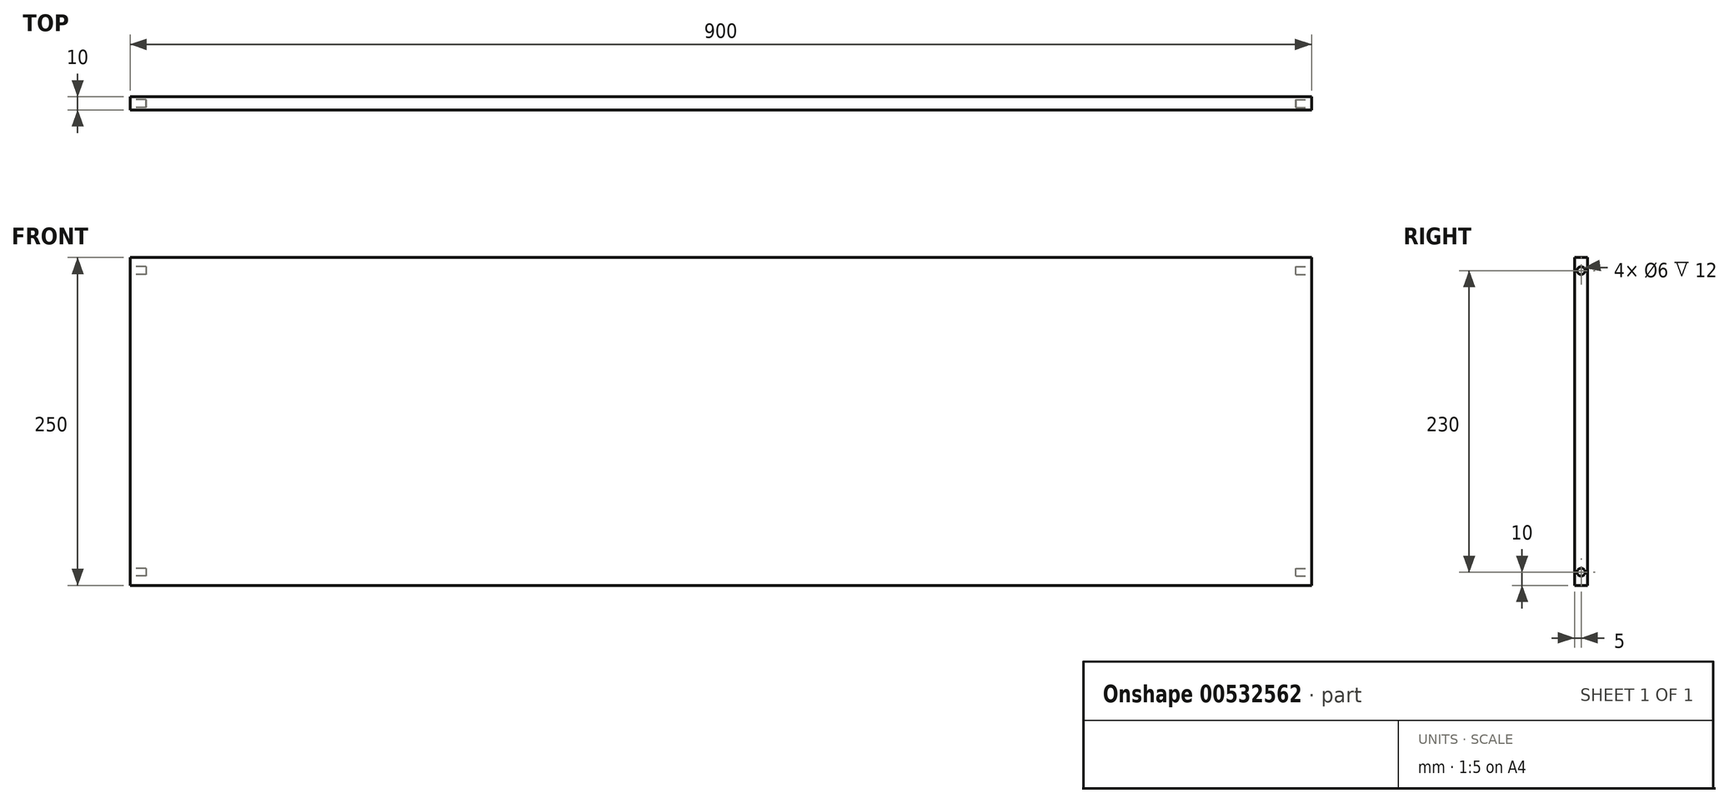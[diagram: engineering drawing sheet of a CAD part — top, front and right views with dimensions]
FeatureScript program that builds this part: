
annotation { "Feature Type Name" : "Feature", "Feature Type Description" : "" }
export const myFeature = defineFeature(function(context is Context, id is Id, definition is map)
    precondition{}
    {
        {
            var Q0;
            Q0=qCreatedBy(makeId("Right.planeOp"),FACE);
            var sketch = newSketch(context, id + "F0", { "sketchPlane" : qUnion([Q0])});
            skLineSegment(sketch, "E0.bottom", {"start": v(0, 0) * mm, "end": v(10, 0) * mm});
            skLineSegment(sketch, "E0.top", {"start": v(0, 250) * mm, "end": v(10, 250) * mm});
            skLineSegment(sketch, "E0.left", {"start": v(0, 0) * mm, "end": v(0, 250) * mm});
            skLineSegment(sketch, "E0.right", {"start": v(10, 0) * mm, "end": v(10, 250) * mm});
            skSolve(sketch);
        }
        {
            var Q0;
            Q0 = qSketchRegion(id + "F0", true);
            extrude(context, id + "F1", {"entities" : qUnion([Q0]), "depth" : 900 * mm, "offsetDistance" : 25 * mm});
        }
        {
            var Q0;
            Q0=makeQuery(id+"F1.opExtrude","CAP_FACE",FACE,{"disambiguationData":[OSD([sQuery(id+"F0.wireOp",EDGE,"E0.bottom"),sQuery(id+"F0.wireOp",EDGE,"E0.top"),sQuery(id+"F0.wireOp",EDGE,"E0.left"),sQuery(id+"F0.wireOp",EDGE,"E0.right")])],"isStart":false});
            var sketch = newSketch(context, id + "F2", { "sketchPlane" : qUnion([Q0])});
            skCircle(sketch, "E1", {"center": v(5, 240) * mm, "radius": 3 * mm});
            skCircle(sketch, "E2", {"center": v(5, 10) * mm, "radius": 3 * mm});
            skSolve(sketch);
        }
        {
            var Q0;
            Q0 = qSketchRegion(id + "F2", true);
            extrude(context, id + "F3", {"entities" : qUnion([Q0]), "operationType" : NewBodyOperationType.REMOVE, "oppositeDirection" : true, "depth" : 12 * mm, "offsetDistance" : 25 * mm});
        }
        {
            var Q0;
            Q0=makeQuery(id+"F1.opExtrude","CAP_FACE",FACE,{"disambiguationData":[OSD([sQuery(id+"F0.wireOp",EDGE,"E0.bottom"),sQuery(id+"F0.wireOp",EDGE,"E0.top"),sQuery(id+"F0.wireOp",EDGE,"E0.left"),sQuery(id+"F0.wireOp",EDGE,"E0.right")])],"isStart":true});
            var sketch = newSketch(context, id + "F4", { "sketchPlane" : qUnion([Q0])});
            skCircle(sketch, "E3", {"center": v(-5, 240) * mm, "radius": 3 * mm});
            skPoint(sketch, "E3.centerSnap0", {"position": v(-5, 250) * mm});
            skCircle(sketch, "E4", {"center": v(-5, 10) * mm, "radius": 3 * mm});
            skSolve(sketch);
        }
        {
            var Q0;
            Q0 = qSketchRegion(id + "F4", true);
            extrude(context, id + "F5", {"entities" : qUnion([Q0]), "operationType" : NewBodyOperationType.REMOVE, "oppositeDirection" : true, "depth" : 12 * mm, "offsetDistance" : 25 * mm});
        }
    });
